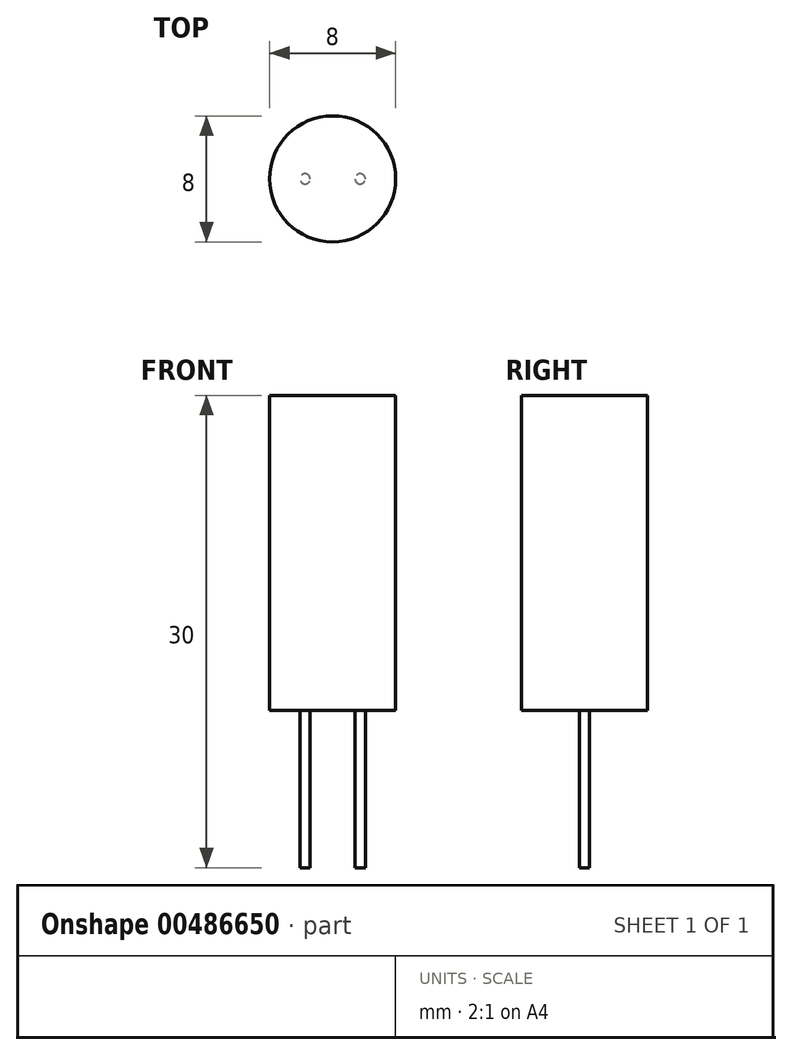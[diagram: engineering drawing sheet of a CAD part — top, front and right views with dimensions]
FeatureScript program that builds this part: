
annotation { "Feature Type Name" : "Feature", "Feature Type Description" : "" }
export const myFeature = defineFeature(function(context is Context, id is Id, definition is map)
    precondition{}
    {
        {
            var Q0;
            Q0=qCreatedBy(makeId("Top.planeOp"),FACE);
            var sketch = newSketch(context, id + "F0", { "sketchPlane" : qUnion([Q0])});
            skCircle(sketch, "E0", {"center": v(0, 0) * mm, "radius": 4 * mm});
            skSolve(sketch);
        }
        {
            var Q0;
            Q0 = qSketchRegion(id + "F0", true);
            extrude(context, id + "F1", {"entities" : qUnion([Q0]), "depth" : 20 * mm});
        }
        {
            var Q0;
            Q0=makeQuery(id+"F1.opExtrude","CAP_FACE",FACE,{"disambiguationData":[OSD([sQuery(id+"F0.wireOp",EDGE,"E0")])],"isStart":true});
            var sketch = newSketch(context, id + "F2", { "sketchPlane" : qUnion([Q0])});
            skCircle(sketch, "E1", {"center": v(-1.75, 0) * mm, "radius": 0.33 * mm});
            skCircle(sketch, "E2", {"center": v(1.75, 0) * mm, "radius": 0.33 * mm});
            skSolve(sketch);
        }
        {
            var Q0;
            Q0 = qSketchRegion(id + "F2", true);
            extrude(context, id + "F3", {"entities" : qUnion([Q0]), "operationType" : NewBodyOperationType.ADD, "depth" : 10 * mm});
        }
    });
